annotation { "Feature Type Name" : "Feature", "Feature Type Description" : "" }
export const myFeature = defineFeature(function(context is Context, id is Id, definition is map)
    precondition{}
    {
        {
            var Q0;
            Q0=qCreatedBy(makeId("Top.planeOp"),FACE);
            var sketch = newSketch(context, id + "F0", { "sketchPlane" : qUnion([Q0])});
            skLineSegment(sketch, "E0.bottom", {"start": v(19.9, -14.3) * mm, "end": v(-19.9, -14.3) * mm});
            skLineSegment(sketch, "E0.top", {"start": v(19.9, 14.3) * mm, "end": v(-19.9, 14.3) * mm});
            skPoint(sketch, "E0.middle", {"position": v(0, 0) * mm});
            skArc(sketch, "E1", {"start": v(-21.6, 13.35) * mm, "mid": v(-25.4, 0) * mm, "end": v(-21.6, -13.35) * mm});
            skArc(sketch, "E2.trimOffspring", {"start": v(21.6, -13.35) * mm, "mid": v(25.4, 0) * mm, "end": v(21.6, 13.35) * mm});
            skPoint(sketch, "E3.orphan", {"position": v(-25.4, -14.3) * mm});
            skPoint(sketch, "E4.orphan", {"position": v(25.4, -14.3) * mm});
            skPoint(sketch, "E5.orphan", {"position": v(25.4, 14.3) * mm});
            skPoint(sketch, "E6.orphan", {"position": v(-25.4, 14.3) * mm});
            skCircle(sketch, "E7", {"center": v(-22, 0) * mm, "radius": 1.6 * mm});
            skPoint(sketch, "E8.visualSharp", {"position": v(21, 14.3) * mm});
            skArc(sketch, "E8.filletArc", {"start": v(21.6, 13.35) * mm, "mid": v(20.88, 14.05) * mm, "end": v(19.9, 14.3) * mm});
            skPoint(sketch, "E9.visualSharp", {"position": v(21, -14.3) * mm});
            skArc(sketch, "E9.filletArc", {"start": v(19.9, -14.3) * mm, "mid": v(20.88, -14.05) * mm, "end": v(21.6, -13.35) * mm});
            skPoint(sketch, "E10.visualSharp", {"position": v(-21, -14.3) * mm});
            skArc(sketch, "E10.filletArc", {"start": v(-21.6, -13.35) * mm, "mid": v(-20.88, -14.05) * mm, "end": v(-19.9, -14.3) * mm});
            skPoint(sketch, "E11.visualSharp", {"position": v(-21, 14.3) * mm});
            skArc(sketch, "E11.filletArc", {"start": v(-19.9, 14.3) * mm, "mid": v(-20.88, 14.05) * mm, "end": v(-21.6, 13.35) * mm});
            skSolve(sketch);
        }
        {
            var Q0;
            Q0=makeQuery(id+"F0.imprint","IMPRINT",FACE,{"disambiguationData":[TD([[makeQuery(id+"F0.imprint","IMPRINT",EDGE,{"derivedFrom":sQuery(id+"F0.wireOp",EDGE,"E0.bottom")}),-1.0]])]});
            extrude(context, id + "F1", {"entities" : qUnion([Q0]), "depth" : 2 * mm});
        }
        {
            var Q0;
            Q0=makeQuery(id+"F1.opExtrude","CAP_FACE",FACE,{"disambiguationData":[OSD([sQuery(id+"F0.wireOp",EDGE,"E0.bottom"),sQuery(id+"F0.wireOp",EDGE,"E0.top"),sQuery(id+"F0.wireOp",EDGE,"E1"),sQuery(id+"F0.wireOp",EDGE,"E2.trimOffspring"),sQuery(id+"F0.wireOp",EDGE,"E7"),sQuery(id+"F0.wireOp",EDGE,"E8.filletArc"),sQuery(id+"F0.wireOp",EDGE,"E9.filletArc"),sQuery(id+"F0.wireOp",EDGE,"E10.filletArc"),sQuery(id+"F0.wireOp",EDGE,"E11.filletArc")])],"isStart":false});
            var sketch = newSketch(context, id + "F2", { "sketchPlane" : qUnion([Q0])});
            skText(sketch, "E12", { "text": "Sonny Lowe\nMakersl.com\nOpenbuilds.org", "fontName": "NotoSansCJKsc-Bold.otf"});
            const initialGuessF2  = {"E12": [-0.0189, 0.00325, 1, 0, 0.00375]};
            skSetInitialGuess(sketch, initialGuessF2);
            skSolve(sketch);
        }
        {
            var Q0;
            Q0 = qSketchRegion(id + "F2", true);
            extrude(context, id + "F3", {"entities" : qUnion([Q0]), "operationType" : NewBodyOperationType.REMOVE, "oppositeDirection" : true, "depth" : 1 * mm});
        }
        {
            var Q0;
            {var subQ0=sQuery(id+"F0.wireOp",EDGE,"E2.trimOffspring");var subQ1=sQuery(id+"F0.wireOp",EDGE,"E1");var subQ2=sQuery(id+"F0.wireOp",EDGE,"E10.filletArc");var subQ3=sQuery(id+"F0.wireOp",EDGE,"E9.filletArc");var subQ4=sQuery(id+"F0.wireOp",EDGE,"E8.filletArc");var subQ5=sQuery(id+"F0.wireOp",EDGE,"E7");var subQ6=sQuery(id+"F0.wireOp",EDGE,"E0.top");var subQ7=sQuery(id+"F0.wireOp",EDGE,"E0.bottom");var subQ8=sQuery(id+"F0.wireOp",EDGE,"E11.filletArc");Q0=makeQuery(id+"F3.boolean.opBoolean","SPLIT",FACE,{"disambiguationData":[TD([makeQuery(id+"F1.opExtrude","SWEPT_FACE",FACE,{"disambiguationData":[OSD([subQ7])]})])],"derivedFrom":makeQuery(id+"F1.opExtrude","CAP_FACE",FACE,{"disambiguationData":[OSD([subQ7,subQ6,subQ1,subQ0,subQ5,subQ4,subQ3,subQ2,subQ8])],"isStart":false})});}
            var sketch = newSketch(context, id + "F4", { "sketchPlane" : qUnion([Q0])});
            skArc(sketch, "E13.0.0", {"start": v(21.6, 13.35) * mm, "mid": v(20.88, 14.05) * mm, "end": v(19.9, 14.3) * mm});
            skLineSegment(sketch, "E13.0.1", {"start": v(19.9, 14.3) * mm, "end": v(-19.9, 14.3) * mm});
            skArc(sketch, "E13.0.2", {"start": v(-19.9, 14.3) * mm, "mid": v(-20.88, 14.05) * mm, "end": v(-21.6, 13.35) * mm});
            skArc(sketch, "E13.0.3", {"start": v(-21.6, 13.35) * mm, "mid": v(-25.4, 0) * mm, "end": v(-21.6, -13.35) * mm});
            skArc(sketch, "E13.0.4", {"start": v(-21.6, -13.35) * mm, "mid": v(-20.88, -14.05) * mm, "end": v(-19.9, -14.3) * mm});
            skLineSegment(sketch, "E13.0.5", {"start": v(-19.9, -14.3) * mm, "end": v(19.9, -14.3) * mm});
            skArc(sketch, "E13.0.6", {"start": v(19.9, -14.3) * mm, "mid": v(20.88, -14.05) * mm, "end": v(21.6, -13.35) * mm});
            skArc(sketch, "E13.0.7", {"start": v(21.6, -13.35) * mm, "mid": v(25.4, 0) * mm, "end": v(21.6, 13.35) * mm});
            skArc(sketch, "E14.0", {"start": v(20.33, -12.56) * mm, "mid": v(23.9, 0) * mm, "end": v(20.33, 12.56) * mm});
            skArc(sketch, "E14.1", {"start": v(19.9, -12.8) * mm, "mid": v(20.15, -12.74) * mm, "end": v(20.33, -12.56) * mm});
            skArc(sketch, "E14.2", {"start": v(20.33, 12.56) * mm, "mid": v(20.15, 12.74) * mm, "end": v(19.9, 12.8) * mm});
            skLineSegment(sketch, "E14.3", {"start": v(-19.9, -12.8) * mm, "end": v(19.9, -12.8) * mm});
            skLineSegment(sketch, "E14.4", {"start": v(19.9, 12.8) * mm, "end": v(-19.9, 12.8) * mm});
            skArc(sketch, "E14.5", {"start": v(-19.9, 12.8) * mm, "mid": v(-20.15, 12.74) * mm, "end": v(-20.33, 12.56) * mm});
            skArc(sketch, "E14.6", {"start": v(-20.33, 12.56) * mm, "mid": v(-23.9, 0) * mm, "end": v(-20.33, -12.56) * mm});
            skArc(sketch, "E14.7", {"start": v(-20.33, -12.56) * mm, "mid": v(-20.15, -12.74) * mm, "end": v(-19.9, -12.8) * mm});
            skArc(sketch, "E15.0", {"start": v(20.76, -12.83) * mm, "mid": v(24.4, 0) * mm, "end": v(20.76, 12.83) * mm});
            skArc(sketch, "E15.1", {"start": v(19.9, -13.3) * mm, "mid": v(20.4, -13.17) * mm, "end": v(20.76, -12.83) * mm});
            skArc(sketch, "E15.2", {"start": v(20.76, 12.83) * mm, "mid": v(20.4, 13.17) * mm, "end": v(19.9, 13.3) * mm});
            skLineSegment(sketch, "E15.3", {"start": v(-19.9, -13.3) * mm, "end": v(19.9, -13.3) * mm});
            skLineSegment(sketch, "E15.4", {"start": v(19.9, 13.3) * mm, "end": v(-19.9, 13.3) * mm});
            skArc(sketch, "E15.5", {"start": v(-19.9, 13.3) * mm, "mid": v(-20.4, 13.17) * mm, "end": v(-20.76, 12.83) * mm});
            skArc(sketch, "E15.6", {"start": v(-20.76, 12.83) * mm, "mid": v(-24.4, 0) * mm, "end": v(-20.76, -12.83) * mm});
            skArc(sketch, "E15.7", {"start": v(-20.76, -12.83) * mm, "mid": v(-20.4, -13.17) * mm, "end": v(-19.9, -13.3) * mm});
            skSolve(sketch);
        }
        {
            var Q0;
            Q0=makeQuery(id+"F4.imprint","IMPRINT",FACE,{"disambiguationData":[TD([[makeQuery(id+"F4.imprint","IMPRINT",EDGE,{"derivedFrom":sQuery(id+"F4.wireOp",EDGE,"E14.0")}),-1.0]])]});
            extrude(context, id + "F5", {"entities" : qUnion([Q0]), "operationType" : NewBodyOperationType.REMOVE, "oppositeDirection" : true, "depth" : .5 * mm});
        }
    });